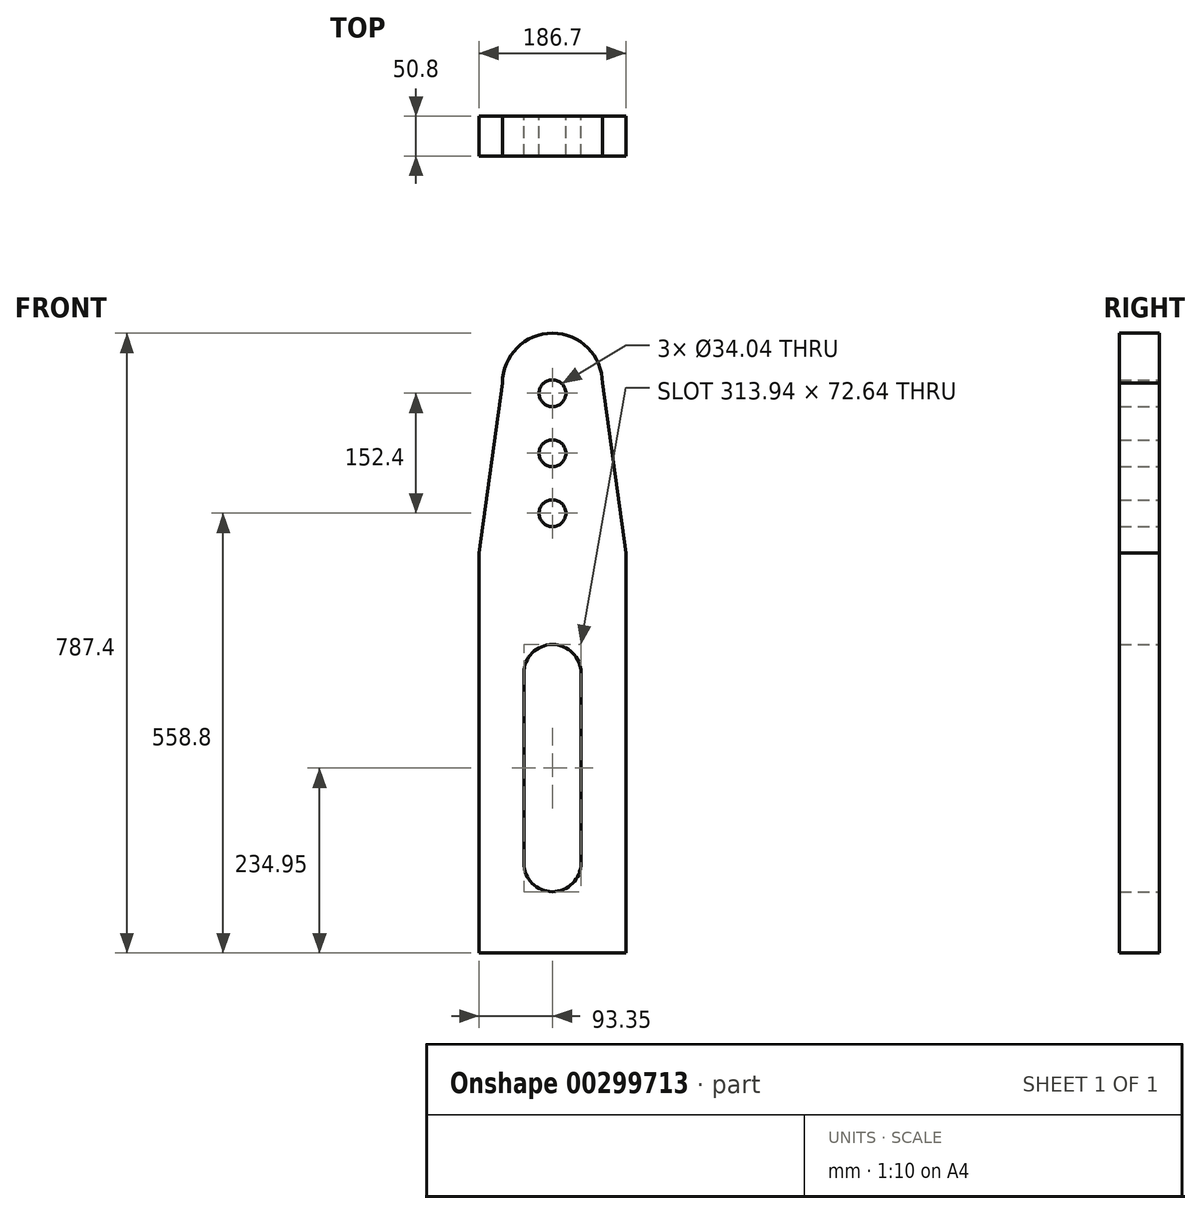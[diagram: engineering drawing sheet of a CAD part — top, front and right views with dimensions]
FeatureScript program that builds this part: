
annotation { "Feature Type Name" : "Feature", "Feature Type Description" : "" }
export const myFeature = defineFeature(function(context is Context, id is Id, definition is map)
    precondition{}
    {
        {
            var Q0;
            Q0=qCreatedBy(makeId("Front.planeOp"),FACE);
            var sketch = newSketch(context, id + "F0", { "sketchPlane" : qUnion([Q0])});
            skLineSegment(sketch, "E0", {"start": v(0, 0) * mm, "end": v(0, 737.18) * mm});
            skLineSegment(sketch, "E1", {"start": v(0, 0) * mm, "end": v(93.35, 0) * mm});
            skLineSegment(sketch, "E2", {"start": v(93.35, 0) * mm, "end": v(93.35, 508) * mm});
            skLineSegment(sketch, "E3", {"start": v(-22.53, 723.9) * mm, "end": v(26.3, 723.9) * mm});
            skArc(sketch, "E4", {"start": v(0, 787.4) * mm, "mid": v(44.9, 768.8) * mm, "end": v(63.5, 723.9) * mm});
            skLineSegment(sketch, "E5", {"start": v(63.5, 723.9) * mm, "end": v(93.34, 508) * mm});
            skCircle(sketch, "E6", {"center": v(0, 711.2) * mm, "radius": 17.02 * mm});
            skCircle(sketch, "E7", {"center": v(0, 635) * mm, "radius": 17.02 * mm});
            skCircle(sketch, "E8", {"center": v(0, 558.8) * mm, "radius": 17.02 * mm});
            skLineSegment(sketch, "E9", {"start": v(-30.05, 355.6) * mm, "end": v(78.87, 355.6) * mm});
            skLineSegment(sketch, "E10", {"start": v(-31.3, 114.3) * mm, "end": v(77.62, 114.3) * mm});
            skArc(sketch, "E11", {"start": v(0, 391.92) * mm, "mid": v(25.68, 381.28) * mm, "end": v(36.32, 355.6) * mm});
            skArc(sketch, "E12", {"start": v(0, 77.98) * mm, "mid": v(25.68, 88.62) * mm, "end": v(36.32, 114.3) * mm});
            skLineSegment(sketch, "E13", {"start": v(36.32, 355.6) * mm, "end": v(36.32, 114.3) * mm});
            skArc(sketch, "E14.MirrorCS", {"start": v(0, 787.4) * mm, "mid": v(-44.9, 768.8) * mm, "end": v(-63.5, 723.9) * mm});
            skLineSegment(sketch, "E15.MirrorCS", {"start": v(-63.5, 723.9) * mm, "end": v(-93.35, 508) * mm});
            skLineSegment(sketch, "E16.MirrorCS", {"start": v(-93.35, 0) * mm, "end": v(-93.35, 508) * mm});
            skLineSegment(sketch, "E17.MirrorCS", {"start": v(0, 0) * mm, "end": v(-93.35, 0) * mm});
            skArc(sketch, "E18.MirrorCS", {"start": v(0, 77.98) * mm, "mid": v(-25.68, 88.62) * mm, "end": v(-36.32, 114.3) * mm});
            skLineSegment(sketch, "E19.MirrorCS", {"start": v(-36.32, 355.6) * mm, "end": v(-36.32, 114.3) * mm});
            skArc(sketch, "E20.MirrorCS", {"start": v(0, 391.92) * mm, "mid": v(-25.68, 381.28) * mm, "end": v(-36.32, 355.6) * mm});
            skSolve(sketch);
        }
        {
            var Q0;
            Q0 = qSketchRegion(id + "F0", true);
            extrude(context, id + "F1", {"entities" : qUnion([Q0]), "depth" : 50.8 * mm});
        }
    });
